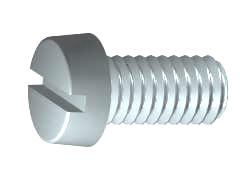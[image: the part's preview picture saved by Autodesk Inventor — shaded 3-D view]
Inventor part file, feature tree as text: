
AUTODESK INVENTOR PART (.ipt)
format: ipt  version: unknown  size: 278,016 bytes
history: native  units: mm (DEFAULTED — no unit token found)
features: other x1, extrude x1, plane x1
ambient origin geometry x7: Origin, YZ Plane, XZ Plane, X Axis, Y Axis, Z Axis, Center Point
feature tree (3):
  other  "Körper"
  extrude  "Loch"  Depth=6.0mm
  plane  "Work Plane1"
